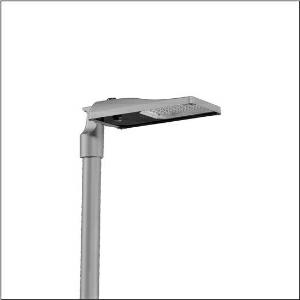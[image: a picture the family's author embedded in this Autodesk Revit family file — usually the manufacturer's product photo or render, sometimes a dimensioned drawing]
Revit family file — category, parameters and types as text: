
# Revit family: streetlight_sl_31_mini___p0_5a_5xh6v31t08ha_7d31
name_source: partatom
category: Lighting Fixtures
units: mm (PartAtom-declared; Revit-internal decimal feet)

## family parameters
Cut with Voids When Loaded = No
Host = Face
Light Source = No
Part Type = Normal
Room Calculation Point = No
Round Connector Dimension = Use Diameter
Shared = No

## types (1)
- --- (1 x LED, 9070 lm, 68.3 W, 3000K)
    Apparent Load = 68 VA
    CIE Flux Codes = 37 73 96 100 100
    Color Rendering = 70
    Color Temperature = 3000K
    Default Elevation = 1800 mm
    Description = Streetlight SL 31 mini D4i, Desk-Remote mast luminaire for post-top, side-entry; light control with lens of PMMA; light distribution: P0.5a, direct asymmetric distribution, for standard-compliant lighting for roads and squares; LED: luminous flux: 9.070lm, light colour: 730, colour temperature: 3000K; luminous efficacy: 132,8lm/W; control: pre-setting: logarithmic dimming characteristic, flexible luminous flux parameterisation, time-dependent luminous flux control, constant luminous flux control, power reduction, intelligent temperature release in ECG and LED module, overheat protection; luminaire housing, of diecast aluminium, Siteco® metallic grey (DB 702S), corrosivity category C5 high according to DIN EN ISO 12944; cover of toughened safety glass, transparent, opened without tools; mast flange of diecast aluminium, Siteco® metallic grey (DB 702S), spigot size: 76/60mm, mast flange included unmounted; with cable H07RN-F 2x 1.5mm², cable length: 8,5m, connection cable pre-assembled; mains connection: 220..240V, AC, 50/60Hz; power consumption (at start of service life): 68,3W / (at end of service life): 74,5W / (with reduced operation 50%): 29,5W; protection rating (complete): IP66; insulation class (complete): insulation class II (safety insulation); impact resistance: IK09; certification: CE, ENEC, ENEC+, VDE, UKCA, ZD4i; permissible operating ambient temperature for outdoor applications: -40..+50°C; packaging unit: 1 piece

Light Distribution: P0.5a
    Height = 76 mm
    Lamp = 1 x LED
    Lamp Light Flux = 9070 lm
    Lamp Power = 68.3 W
    Lamp count = 1
    Length = 547 mm
    Luminous efficacy = 133 lm/W
    Manufacturer = Siteco
    ModVariant = No
    Model = 5XH6V31T08HA
    Number of Poles = 1
    OnlyDefault = Yes
    Power Factor = 1
    Product Name = Streetlight SL 31 mini | P0.5a
    Product group = mast luminaire | pylon top
    ProductGroupID = 6100
    Protection Class = Protection class II
    Protection Degree = IP 66
    RLX_Detail_Level = 1
    RLX_Emergency_Light_Flux = 0 lm
    RLX_Emergency_Type = 0
    RLX_Emergency_Type_DB = No
    RlxData = <blob elided: 23833 chars, md5=ed4db3a6>
    Socket = socket
    Standby Power = 0 W
    System Light Flux = 9070 lm
    System Power = 68 W
    Type Comments = factory setting: luminous flux: 100 % | dim-lin: 254 | 692 mA
    Type Image = l_1300332.jpg
    URL = http://relux.com
    VarID = @adj_006567
    Voltage = 0 V
    Weight = 0.00 kg
    Width = 265 mm

## geometry (parser evidence)
native form markers: Blend x4, Sweep x11
no freeform markers — native parametric forms only
